# Revit family: Heater-QMARK-FRP_FRS_Series_Infrared
name_source: partatom
category: Mechanical Equipment
units: mm (PartAtom-declared; Revit-internal decimal feet)

## family parameters
Classification = None
Cut with Voids When Loaded = No
Host = Face
Part Type = Normal
Room Calculation Point = No
Round Connector Dimension = Use Diameter
Shared = No

## types (12) — shared parameters
Between Heaters Clearance = 3' - 0"
Brand = QMark
Bulb Material = Metal Sheath , Quartz Tube and Quartz Lamp
Bulb Sleeves = Included or Not Included
Ceiling Clearance = 0' - 6"
Default Elevation = 0' - 0 3/16"
Description = Infrared Heater
Instruction Sheet Link = https://www.marleymep.com
Layout = Custom
Manufacturer = Marley® Engineered Products
Mounting Bracket = Wall Bracket, Tilt Bracket or Not Included
Number of Poles = 1
Phase = 1
Power Factor = 1
Product Documentation Link = https://www.marleymep.com
Product Generation = C
Product Name = FRP/FRS Series - Infrared Heater
Product Page URL = https://www.marleymep.com
Recessed Trim Kit = Included or Not Included
Recessed Trim Kit Finish = Bronze, Brushed Stainless Steel, White or Custom
Reflection Angle = 30° Symmetrical, 60° Symmetrical, 60° Asymmetrical and 90° Symmetrical
Side Walls Clearance = 2' - 0"
To Floor Clearance = 7' - 0"
Total Heating Capacity = 5800.0 Btu/h
URL = https://www.marleymep.com
Unit Finish = Bronze, Brushed Stainless Steel or Custom
Version = 2020 - v1.0b
Voltage = 480 V
Watts = 1700 W
Wire Guards = Included or Not Included

## per-type parameters (varying)
| type | Bulb Quantity | Elements Type | Height | Length | Model | Width |
| FRP2 - 2 Bulbs - 017 kW - 208 V | 2 | 2 Elements | 0' - 8 17/32" | 2' - 0 3/8" | FRP2 | 1' - 7 7/8" |
| FRP3 - 2 Bulbs - 017 kW - 208 V | 2 | 2 Elements | 0' - 8 17/32" | 2' - 9 3/8" | FRP3 | 1' - 7 7/8" |
| FRP4 - 2 Bulbs - 017 kW - 208 V | 2 | 2 Elements | 0' - 8 17/32" | 3' - 10 3/8" | FRP4 | 1' - 7 7/8" |
| FRS2 - 2 Bulbs - 017 kW - 208 V | 2 | 2 Elements | 0' - 8 17/32" | 2' - 0 3/8" | FRS2 | 1' - 7 7/8" |
| FRS3 - 2 Bulbs - 017 kW - 208 V | 2 | 2 Elements | 0' - 8 17/32" | 2' - 9 3/8" | FRS3 | 1' - 7 7/8" |
| FRS4 - 2 Bulbs - 017 kW - 208 V | 2 | 2 Elements | 0' - 8 17/32" | 3' - 10 3/8" | FRS4 | 1' - 7 7/8" |
| FRP2 - 3 Bulbs - 017 kW - 208 V | 3 | 3 Elements | 0' - 9 5/32" | 2' - 0 3/8" | FRP2 | 2' - 2 5/16" |
| FRP3 - 3 Bulbs - 017 kW - 208 V | 3 | 3 Elements | 0' - 9 5/32" | 2' - 9 3/8" | FRP3 | 2' - 2 5/16" |
| FRP4 - 3 Bulbs - 017 kW - 208 V | 3 | 3 Elements | 0' - 9 5/32" | 3' - 10 3/8" | FRP4 | 2' - 2 5/16" |
| FRS2 - 3 Bulbs - 017 kW - 208 V | 3 | 3 Elements | 0' - 9 5/32" | 2' - 0 3/8" | FRS2 | 2' - 2 5/16" |
| FRS3 - 3 Bulbs - 017 kW - 208 V | 3 | 3 Elements | 0' - 9 5/32" | 2' - 9 3/8" | FRS3 | 2' - 2 5/16" |
| FRS4 - 3 Bulbs - 017 kW - 208 V | 3 | 3 Elements | 0' - 9 5/32" | 3' - 10 3/8" | FRS4 | 2' - 2 5/16" |

## geometry (parser evidence)
native form markers: Sweep x8
no freeform markers — native parametric forms only
